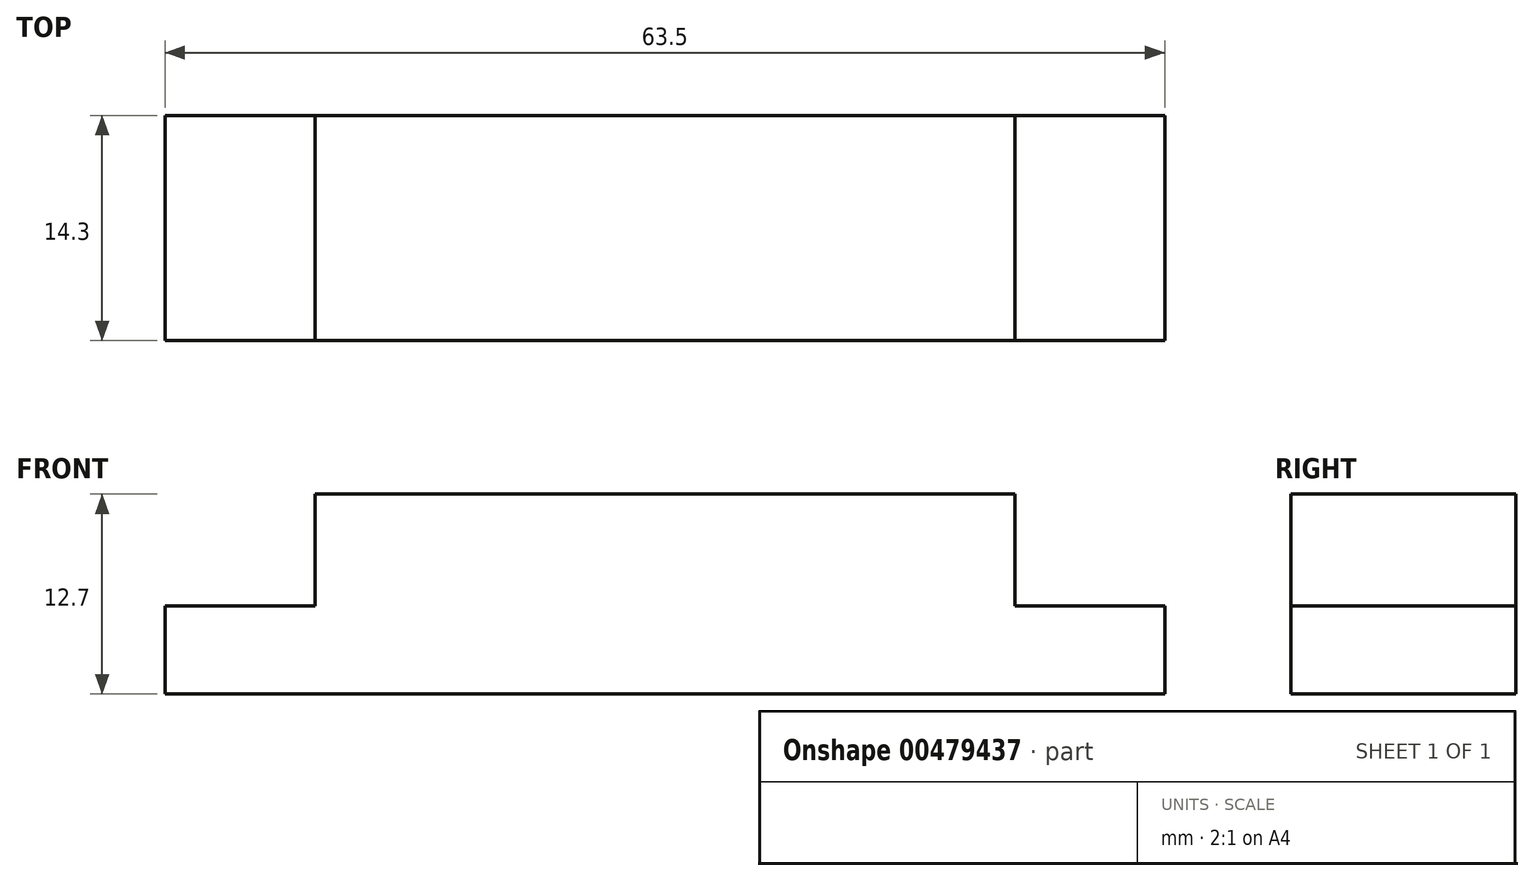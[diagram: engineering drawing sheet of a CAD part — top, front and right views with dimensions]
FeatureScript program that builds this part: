
annotation { "Feature Type Name" : "Feature", "Feature Type Description" : "" }
export const myFeature = defineFeature(function(context is Context, id is Id, definition is map)
    precondition{}
    {
        {
            var Q0;
            Q0=qCreatedBy(makeId("Top.planeOp"),FACE);
            var sketch = newSketch(context, id + "F0", { "sketchPlane" : qUnion([Q0])});
            skLineSegment(sketch, "E0.bottom", {"start": v(0, 0) * mm, "end": v(63.5, 0) * mm});
            skLineSegment(sketch, "E0.top", {"start": v(0, 14.3) * mm, "end": v(63.5, 14.3) * mm});
            skLineSegment(sketch, "E0.left", {"start": v(0, 0) * mm, "end": v(0, 14.3) * mm});
            skLineSegment(sketch, "E0.right", {"start": v(63.5, 0) * mm, "end": v(63.5, 14.3) * mm});
            skLineSegment(sketch, "E1", {"start": v(9.53, 0) * mm, "end": v(9.53, 14.3) * mm});
            skLineSegment(sketch, "E2", {"start": v(53.98, 0) * mm, "end": v(53.98, 14.3) * mm});
            skSolve(sketch);
        }
        {
            var Q0;
            {var subQ0=sQuery(id+"F0.wireOp",EDGE,"E1");Q0=makeQuery(id+"F0.imprint","IMPRINT",FACE,{"disambiguationData":[TD([[makeQuery(id+"F0.imprint","IMPRINT",EDGE,{"derivedFrom":subQ0}),-1.0]])]});}
            extrude(context, id + "F1", {"entities" : qUnion([Q0]), "depth" : 12.7 * mm, "offsetDistance" : 25.4 * mm});
        }
        {
            var Q0;
            {var subQ0=sQuery(id+"F0.wireOp",EDGE,"E0.left");Q0=makeQuery(id+"F0.imprint","IMPRINT",FACE,{"disambiguationData":[TD([[makeQuery(id+"F0.imprint","IMPRINT",EDGE,{"derivedFrom":subQ0}),-1.0]])]});}
            var Q1;
            {var subQ0=sQuery(id+"F0.wireOp",EDGE,"E0.right");Q1=makeQuery(id+"F0.imprint","IMPRINT",FACE,{"disambiguationData":[TD([[makeQuery(id+"F0.imprint","IMPRINT",EDGE,{"derivedFrom":subQ0}),1.0]])]});}
            extrude(context, id + "F2", {"entities" : qUnion([Q0, Q1]), "operationType" : NewBodyOperationType.ADD, "depth" : 5.6 * mm, "offsetDistance" : 25.4 * mm});
        }
    });
